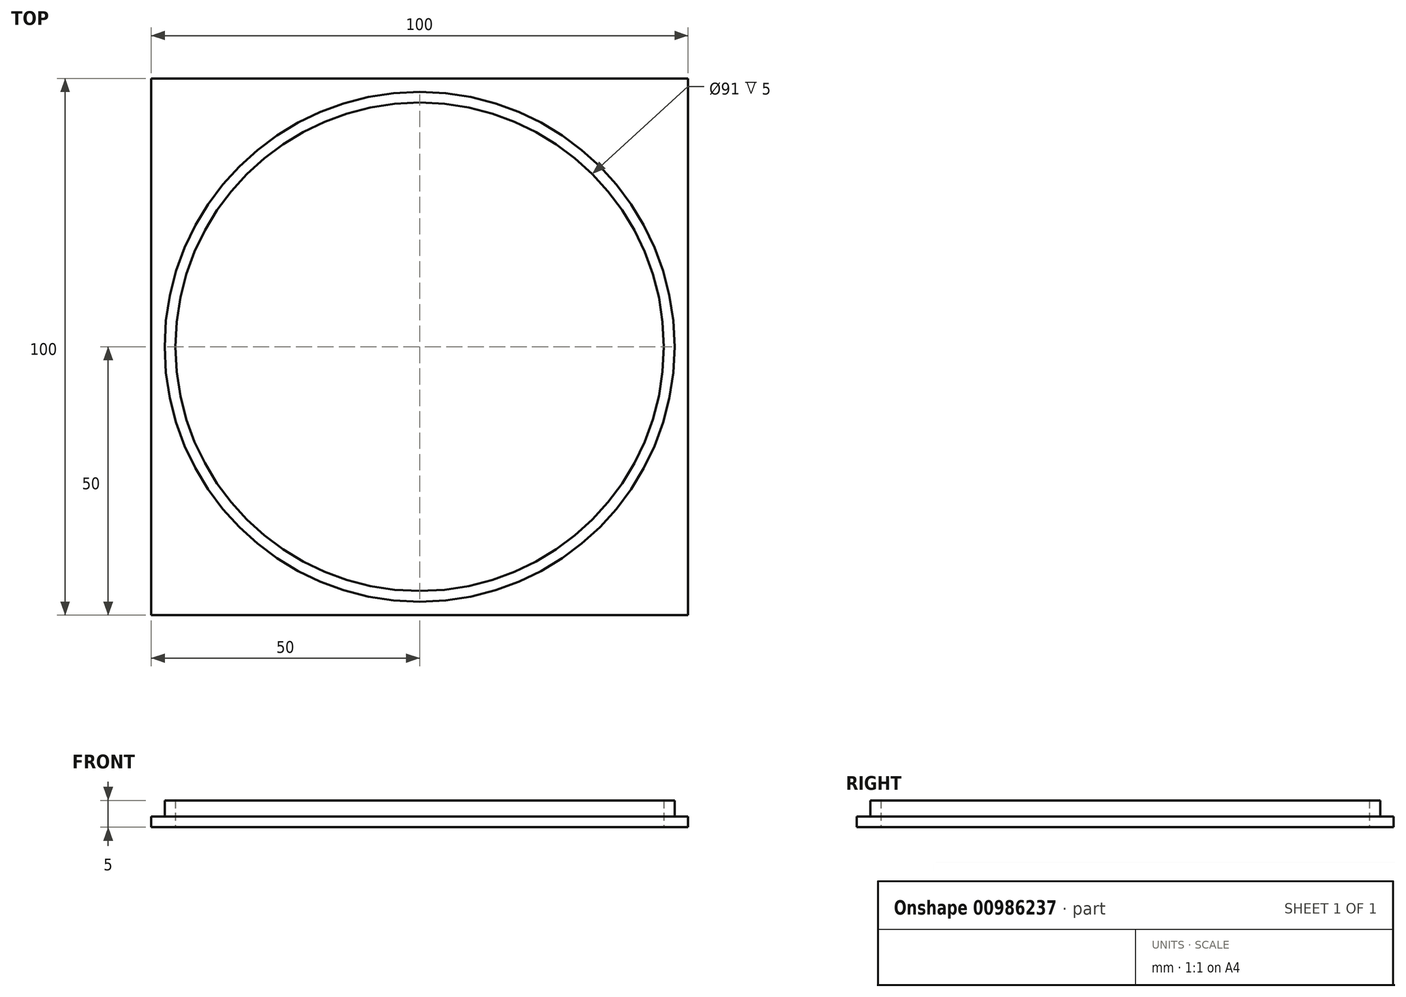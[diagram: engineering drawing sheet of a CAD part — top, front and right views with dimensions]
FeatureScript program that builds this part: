
annotation { "Feature Type Name" : "Feature", "Feature Type Description" : "" }
export const myFeature = defineFeature(function(context is Context, id is Id, definition is map)
    precondition{}
    {
        {
            var Q0;
            Q0=qCreatedBy(makeId("Top.planeOp"),FACE);
            var sketch = newSketch(context, id + "F0", { "sketchPlane" : qUnion([Q0])});
            skCircle(sketch, "E0", {"center": v(0, 0) * mm, "radius": 47.5 * mm});
            skCircle(sketch, "E1.0", {"center": v(0, 0) * mm, "radius": 45.5 * mm});
            skSolve(sketch);
        }
        {
            var Q0;
            Q0 = qSketchRegion(id + "F0", true);
            extrude(context, id + "F1", {"entities" : qUnion([Q0]), "depth" : 3 * mm, "offsetDistance" : 25 * mm});
        }
        {
            var Q0;
            Q0=qCreatedBy(makeId("Top.planeOp"),FACE);
            var sketch = newSketch(context, id + "F2", { "sketchPlane" : qUnion([Q0])});
            skLineSegment(sketch, "E2.bottom", {"start": v(-50, 50) * mm, "end": v(50, 50) * mm});
            skLineSegment(sketch, "E2.top", {"start": v(-50, -50) * mm, "end": v(50, -50) * mm});
            skLineSegment(sketch, "E2.left", {"start": v(-50, 50) * mm, "end": v(-50, -50) * mm});
            skLineSegment(sketch, "E2.right", {"start": v(50, 50) * mm, "end": v(50, -50) * mm});
            skLineSegment(sketch, "E3", {"start": v(-50, 0) * mm, "end": v(50, 0) * mm, "construction": true});
            skLineSegment(sketch, "E4", {"start": v(0, 50) * mm, "end": v(0, -50) * mm, "construction": true});
            skCircle(sketch, "E5", {"center": v(0, 0) * mm, "radius": 45.5 * mm});
            skSolve(sketch);
        }
        {
            var Q0;
            Q0=makeQuery(id+"F2.imprint","IMPRINT",FACE,{"disambiguationData":[TD([[makeQuery(id+"F2.imprint","IMPRINT",EDGE,{"derivedFrom":sQuery(id+"F2.wireOp",EDGE,"E2.bottom")}),-1.0]])]});
            extrude(context, id + "F3", {"entities" : qUnion([Q0]), "operationType" : NewBodyOperationType.ADD, "oppositeDirection" : true, "depth" : 2 * mm, "offsetDistance" : 25 * mm});
        }
    });
